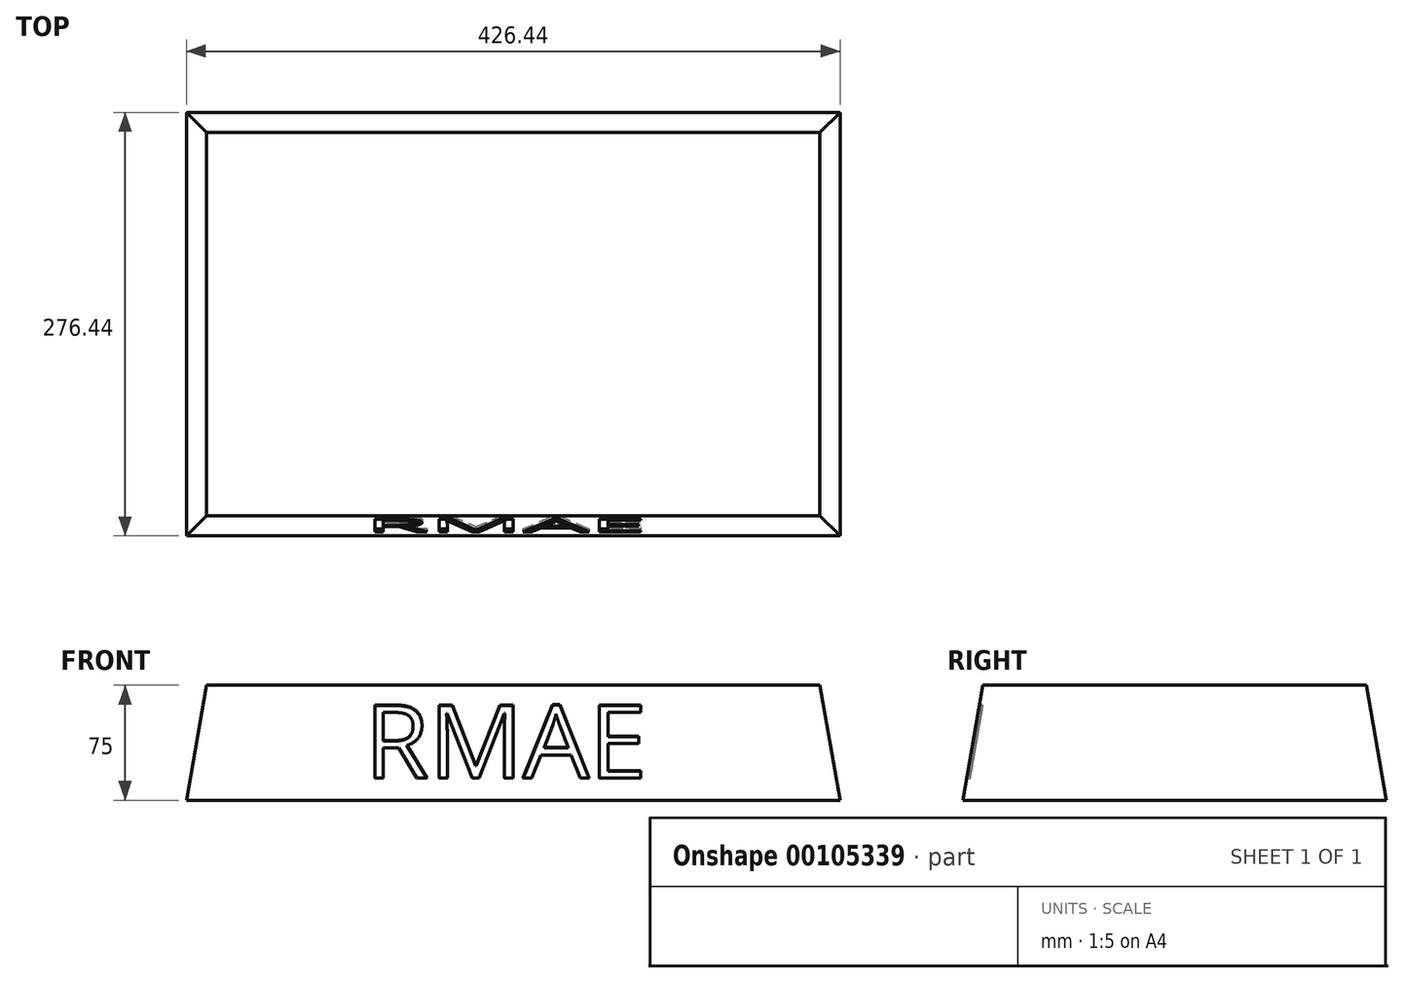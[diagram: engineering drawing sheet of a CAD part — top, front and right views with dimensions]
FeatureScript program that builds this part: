
annotation { "Feature Type Name" : "Feature", "Feature Type Description" : "" }
export const myFeature = defineFeature(function(context is Context, id is Id, definition is map)
    precondition{}
    {
        {
            var Q0;
            Q0=qCreatedBy(makeId("Top.planeOp"),FACE);
            var sketch = newSketch(context, id + "F0", { "sketchPlane" : qUnion([Q0])});
            skLineSegment(sketch, "E0.bottom", {"start": v(200, -125) * mm, "end": v(-200, -125) * mm});
            skLineSegment(sketch, "E0.top", {"start": v(200, 125) * mm, "end": v(-200, 125) * mm});
            skLineSegment(sketch, "E0.left", {"start": v(200, -125) * mm, "end": v(200, 125) * mm});
            skLineSegment(sketch, "E0.right", {"start": v(-200, -125) * mm, "end": v(-200, 125) * mm});
            skPoint(sketch, "E0.middle", {"position": v(0, 0) * mm});
            skSolve(sketch);
        }
        {
            var Q0;
            Q0 = qSketchRegion(id + "F0", true);
            extrude(context, id + "F1", {"entities" : qUnion([Q0]), "oppositeDirection" : true, "depth" : 75 * mm, "hasDraft" : true, "draftAngle" : 10 * degree});
        }
        {
            var Q0;
            Q0=makeQuery(id+"F1.opExtrude","SWEPT_FACE",FACE,{"disambiguationData":[OSD([sQuery(id+"F0.wireOp",EDGE,"E0.bottom")])]});
            var sketch = newSketch(context, id + "F2", { "sketchPlane" : qUnion([Q0])});
            skText(sketch, "E1", { "text": "RMAE", "fontName": "OpenSans-Regular.ttf"});
            const initialGuessF2  = {"E1": [-0.097, -0.08333, 1, 0, 0.04897]};
            skSetInitialGuess(sketch, initialGuessF2);
            skSolve(sketch);
        }
        {
            var Q0;
            Q0 = qSketchRegion(id + "F2", true);
            extrude(context, id + "F3", {"entities" : qUnion([Q0]), "operationType" : NewBodyOperationType.REMOVE, "oppositeDirection" : true, "depth" : 2 * mm});
        }
    });
